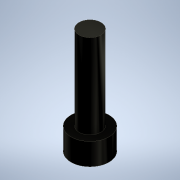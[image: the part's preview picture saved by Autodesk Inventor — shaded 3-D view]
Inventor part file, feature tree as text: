
AUTODESK INVENTOR PART (.ipt)
format: ipt  version: 2020.2 (Build 242310000, 310)  size: 98,816 bytes
history: native  units: mm
features: extrude x2, sketch x2, other x1
ambient origin geometry x8: Origin, YZ Plane, XZ Plane, XY Plane, X Axis, Y Axis, Z Axis, Center Point
bodies: Body1 (feature_tree)
feature tree (5):
  other  "ソリッド1"
  extrude  "押し出し1"  Depth=4.5mm
  extrude  "押し出し2"  Depth=2.6mm TaperAngle=0.0deg
  sketch  "スケッチ1"
  sketch  "スケッチ2"
